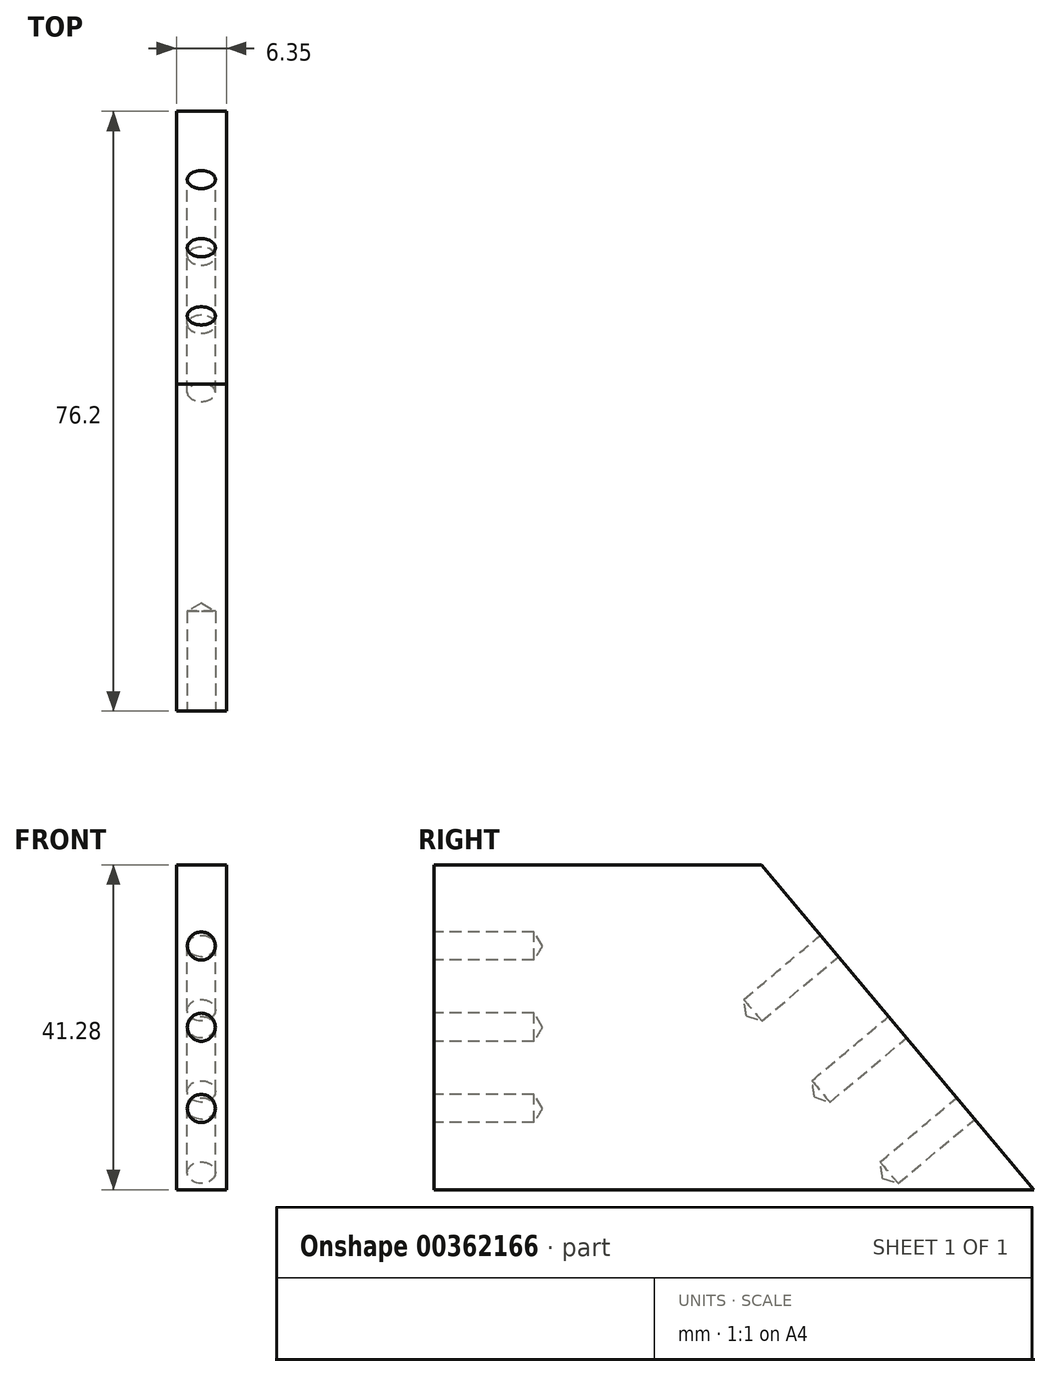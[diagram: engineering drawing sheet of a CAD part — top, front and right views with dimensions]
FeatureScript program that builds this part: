
annotation { "Feature Type Name" : "Feature", "Feature Type Description" : "" }
export const myFeature = defineFeature(function(context is Context, id is Id, definition is map)
    precondition{}
    {
        {
            var Q0;
            Q0=qCreatedBy(makeId("Right.planeOp"),FACE);
            var sketch = newSketch(context, id + "F0", { "sketchPlane" : qUnion([Q0])});
            skLineSegment(sketch, "E0", {"start": v(0, 0) * mm, "end": v(76.2, 0) * mm});
            skLineSegment(sketch, "E1", {"start": v(76.2, 0) * mm, "end": v(41.57, 41.28) * mm});
            skLineSegment(sketch, "E2", {"start": v(41.57, 41.28) * mm, "end": v(0, 41.28) * mm});
            skLineSegment(sketch, "E3", {"start": v(0, 41.27) * mm, "end": v(0, 0) * mm});
            skSolve(sketch);
        }
        {
            var Q0;
            Q0=makeQuery(id+"F0.imprint","IMPRINT",FACE,{"disambiguationData":[TD([[makeQuery(id+"F0.imprint","IMPRINT",EDGE,{"derivedFrom":sQuery(id+"F0.wireOp",EDGE,"E0")}),1.0]])]});
            extrude(context, id + "F1", {"entities" : qUnion([Q0]), "depth" : 6.35 * mm});
        }
        {
            var Q0;
            Q0=makeQuery(id+"F1.opExtrude","SWEPT_FACE",FACE,{"disambiguationData":[OSD([sQuery(id+"F0.wireOp",EDGE,"E1")])]});
            var sketch = newSketch(context, id + "F2", { "sketchPlane" : qUnion([Q0])});
            skLineSegment(sketch, "E4", {"start": v(0, -22.04) * mm, "end": v(-6.35, -22.04) * mm, "construction": true});
            skLineSegment(sketch, "E5", {"start": v(-3.18, 4.9) * mm, "end": v(-3.17, -22.04) * mm, "construction": true});
            skLineSegment(sketch, "E6", {"start": v(-3.18, -22.04) * mm, "end": v(-3.18, -48.98) * mm, "construction": true});
            skPoint(sketch, "E7", {"position": v(-3.18, -8.57) * mm});
            skPoint(sketch, "E8", {"position": v(-3.17, -22.04) * mm});
            skPoint(sketch, "E9", {"position": v(-3.17, -35.51) * mm});
            skSolve(sketch);
        }
        {
            var Q0;
            Q0=makeQuery(id+"F1.opExtrude","SWEPT_FACE",FACE,{"disambiguationData":[OSD([sQuery(id+"F0.wireOp",EDGE,"E3")])]});
            var sketch = newSketch(context, id + "F3", { "sketchPlane" : qUnion([Q0])});
            skLineSegment(sketch, "E10", {"start": v(6.35, 20.64) * mm, "end": v(0, 20.64) * mm, "construction": true});
            skLineSegment(sketch, "E11", {"start": v(3.18, 41.28) * mm, "end": v(3.18, 20.64) * mm, "construction": true});
            skLineSegment(sketch, "E12", {"start": v(3.18, 20.64) * mm, "end": v(3.18, 0) * mm, "construction": true});
            skPoint(sketch, "E13", {"position": v(3.18, 30.96) * mm});
            skPoint(sketch, "E14", {"position": v(3.18, 10.32) * mm});
            skSolve(sketch);
        }
        {
            var Q0;
            Q0=sQuery(id+"F3.wireOp",VERTEX,"E13");
            var Q1;
            Q1=sQuery(id+"F3.wireOp",VERTEX,"E14");
            var Q2;
            Q2=sQuery(id+"F3.wireOp",VERTEX,"E12.start");
            var Q3;
            Q3=makeQuery(id+"F1.opExtrude","SWEPT_BODY",BODY,{"disambiguationData":[OSD([sQuery(id+"F0.wireOp",EDGE,"E0"),sQuery(id+"F0.wireOp",EDGE,"E1"),sQuery(id+"F0.wireOp",EDGE,"E2"),sQuery(id+"F0.wireOp",EDGE,"E3")])]});
            hole(context, id + "F4", {"style" : HoleStyle.SIMPLE, "endStyle" : HoleEndStyle.BLIND, "holeDiameter" : 3.57 * mm, "holeDepth" : 12.7 * mm, "isTappedThrough" : true, "tappedDepth" : 12.7 * mm, "tapClearance" : 3, "startFromSketch" : true, "locations" : qUnion([Q0, Q1, Q2]), "scope" : qUnion([Q3])});
        }
        {
            var Q0;
            Q0=sQuery(id+"F2.wireOp",VERTEX,"E7");
            var Q1;
            Q1=sQuery(id+"F2.wireOp",VERTEX,"E8");
            var Q2;
            Q2=sQuery(id+"F2.wireOp",VERTEX,"E9");
            var Q3;
            Q3=makeQuery(id+"F1.opExtrude","SWEPT_BODY",BODY,{"disambiguationData":[OSD([sQuery(id+"F0.wireOp",EDGE,"E0"),sQuery(id+"F0.wireOp",EDGE,"E1"),sQuery(id+"F0.wireOp",EDGE,"E2"),sQuery(id+"F0.wireOp",EDGE,"E3")])]});
            hole(context, id + "F5", {"style" : HoleStyle.SIMPLE, "endStyle" : HoleEndStyle.BLIND, "holeDiameter" : 3.57 * mm, "holeDepth" : 12.7 * mm, "isTappedThrough" : true, "tappedDepth" : 12.7 * mm, "tapClearance" : 3, "startFromSketch" : true, "locations" : qUnion([Q0, Q1, Q2]), "scope" : qUnion([Q3])});
        }
    });
